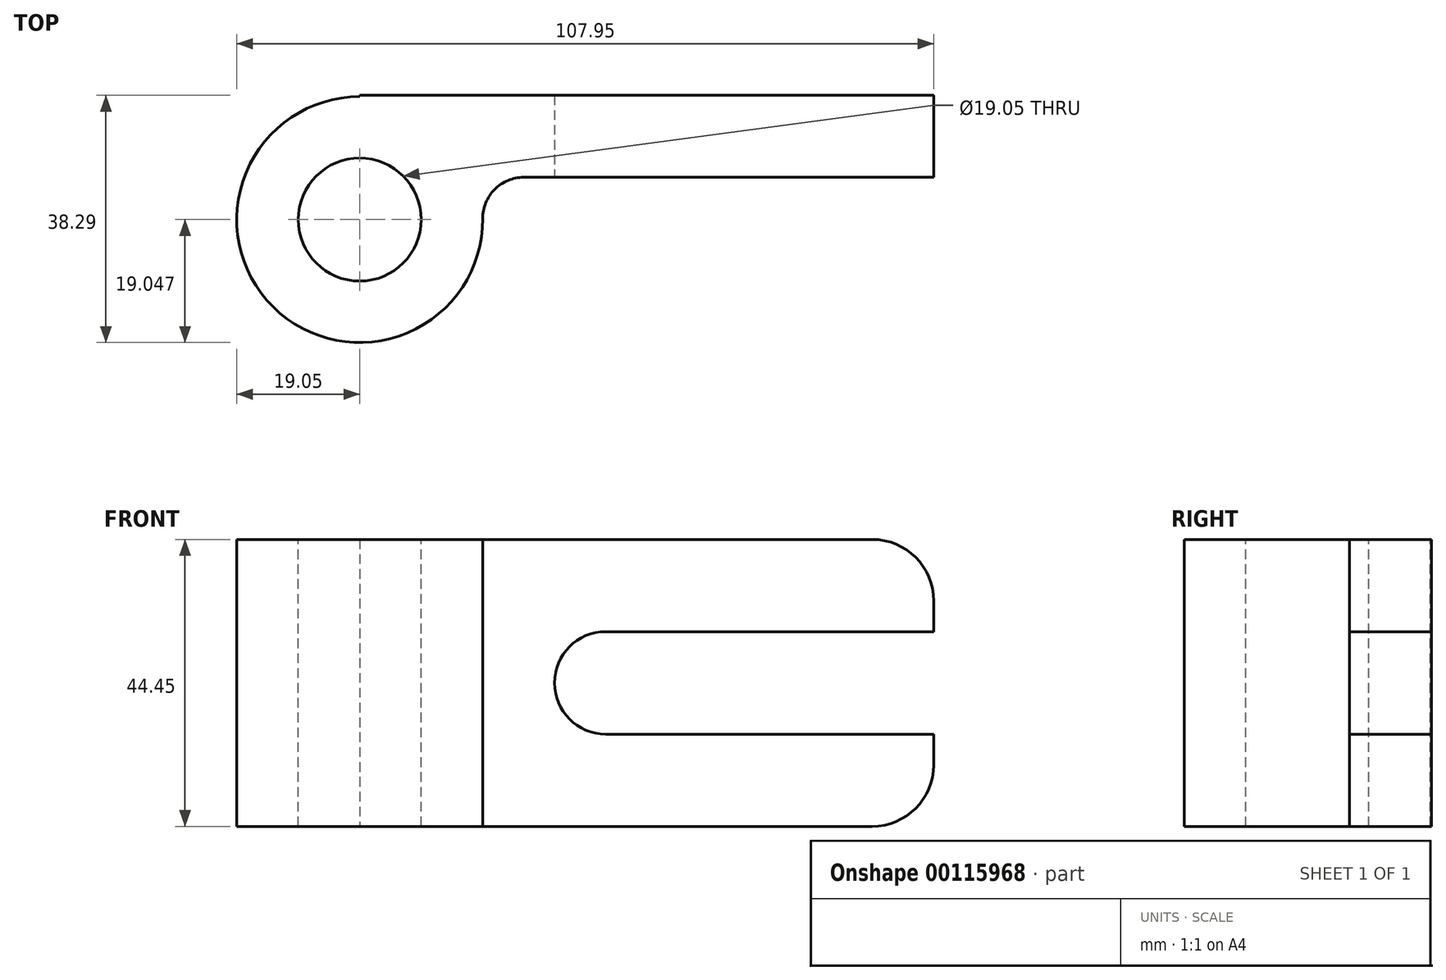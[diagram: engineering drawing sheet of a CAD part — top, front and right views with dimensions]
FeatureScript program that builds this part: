
annotation { "Feature Type Name" : "Feature", "Feature Type Description" : "" }
export const myFeature = defineFeature(function(context is Context, id is Id, definition is map)
    precondition{}
    {
        {
            var Q0;
            Q0=qCreatedBy(makeId("Front.planeOp"),FACE);
            var sketch = newSketch(context, id + "F0", { "sketchPlane" : qUnion([Q0])});
            skLineSegment(sketch, "E0.bottom", {"start": v(0, 8.31) * mm, "end": v(88.9, 8.31) * mm});
            skLineSegment(sketch, "E0.top", {"start": v(0, -36.14) * mm, "end": v(88.9, -36.14) * mm});
            skLineSegment(sketch, "E0.left", {"start": v(0, 8.31) * mm, "end": v(0, -36.14) * mm});
            skLineSegment(sketch, "E0.right", {"start": v(88.9, 8.31) * mm, "end": v(88.9, -36.14) * mm});
            skSolve(sketch);
        }
        {
            var Q0;
            Q0 = qSketchRegion(id + "F0", true);
            extrude(context, id + "F1", {"entities" : qUnion([Q0]), "depth" : 12.7 * mm});
        }
        {
            var Q0;
            Q0=makeQuery(id+"F1.opExtrude","SWEPT_EDGE",EDGE,{"disambiguationData":[OSD([sQuery(id+"F0.wireOp",EDGE,"E0.bottom"),sQuery(id+"F0.wireOp",EDGE,"E0.right")])]});
            var Q1;
            Q1=makeQuery(id+"F1.opExtrude","SWEPT_EDGE",EDGE,{"disambiguationData":[OSD([sQuery(id+"F0.wireOp",EDGE,"E0.top"),sQuery(id+"F0.wireOp",EDGE,"E0.right")])]});
            fillet(context, id + "F2", {"entities" : qUnion([Q0, Q1]), "radius" : 9.52 * mm, "tangentPropagation" : true, "allowEdgeOverflow" : false});
        }
        {
            var Q0;
            Q0=makeQuery(id+"F1.opExtrude","CAP_FACE",FACE,{"disambiguationData":[OSD([sQuery(id+"F0.wireOp",EDGE,"E0.bottom"),sQuery(id+"F0.wireOp",EDGE,"E0.top"),sQuery(id+"F0.wireOp",EDGE,"E0.left"),sQuery(id+"F0.wireOp",EDGE,"E0.right")])],"isStart":false});
            var sketch = newSketch(context, id + "F3", { "sketchPlane" : qUnion([Q0])});
            skCircle(sketch, "E1", {"center": v(38.1, -13.91) * mm, "radius": 7.94 * mm});
            skLineSegment(sketch, "E2", {"start": v(38.1, -5.97) * mm, "end": v(88.9, -5.97) * mm});
            skLineSegment(sketch, "E3", {"start": v(38.1, -21.85) * mm, "end": v(88.9, -21.85) * mm});
            skLineSegment(sketch, "E4", {"start": v(88.9, -21.85) * mm, "end": v(88.9, -5.97) * mm});
            skSolve(sketch);
        }
        {
            var Q0;
            Q0 = qSketchRegion(id + "F3", true);
            extrude(context, id + "F4", {"entities" : qUnion([Q0]), "operationType" : NewBodyOperationType.REMOVE, "oppositeDirection" : true, "depth" : 12.7 * mm});
        }
        {
            var Q0;
            Q0=makeQuery(id+"F1.opExtrude","SWEPT_FACE",FACE,{"disambiguationData":[OSD([sQuery(id+"F0.wireOp",EDGE,"E0.bottom")])]});
            var sketch = newSketch(context, id + "F5", { "sketchPlane" : qUnion([Q0])});
            skCircle(sketch, "E5", {"center": v(0, -19.24) * mm, "radius": 19.05 * mm});
            skCircle(sketch, "E6", {"center": v(0, -19.24) * mm, "radius": 9.53 * mm});
            skSolve(sketch);
        }
        {
            var Q0;
            Q0 = qSketchRegion(id + "F5", true);
            extrude(context, id + "F6", {"entities" : qUnion([Q0]), "operationType" : NewBodyOperationType.ADD, "oppositeDirection" : true, "depth" : 44.45 * mm});
        }
        {
            var Q0;
            Q0=makeQuery(id+"F6.boolean.opBoolean","MERGE",FACE,{"derivedFrom":[makeQuery(id+"F1.opExtrude","SWEPT_FACE",FACE,{"disambiguationData":[OSD([sQuery(id+"F0.wireOp",EDGE,"E0.bottom")])]}),makeQuery(id+"F6.opExtrude","CAP_FACE",FACE,{"disambiguationData":[OSD([sQuery(id+"F5.wireOp",EDGE,"E5"),sQuery(id+"F5.wireOp",EDGE,"E6")])],"isStart":true})]});
            var sketch = newSketch(context, id + "F7", { "sketchPlane" : qUnion([Q0])});
            skCircle(sketch, "E7", {"center": v(0, -19.24) * mm, "radius": 9.53 * mm});
            skSolve(sketch);
        }
        {
            var Q0;
            Q0 = qSketchRegion(id + "F7", true);
            extrude(context, id + "F8", {"entities" : qUnion([Q0]), "operationType" : NewBodyOperationType.REMOVE, "oppositeDirection" : true, "depth" : 44.45 * mm});
        }
        {
            var Q0;
            Q0=makeQuery(id+"F6.boolean.opBoolean","INTERSECT",EDGE,{"derivedFrom":[makeQuery(id+"F1.opExtrude","CAP_FACE",FACE,{"disambiguationData":[OSD([sQuery(id+"F0.wireOp",EDGE,"E0.bottom"),sQuery(id+"F0.wireOp",EDGE,"E0.top"),sQuery(id+"F0.wireOp",EDGE,"E0.left"),sQuery(id+"F0.wireOp",EDGE,"E0.right")])],"isStart":false}),makeQuery(id+"F6.opExtrude","SWEPT_FACE",FACE,{"disambiguationData":[OSD([sQuery(id+"F5.wireOp",EDGE,"E5")])]})]});
            fillet(context, id + "F9", {"entities" : qUnion([Q0]), "radius" : 6.35 * mm, "tangentPropagation" : true, "allowEdgeOverflow" : false});
        }
    });
